# Revit family: Elite_XX_Custom
name_source: partatom
category: Windows
revit_build: Autodesk Revit 2014 (Build: 20130308_1515(x64)
units: mm (PartAtom-declared; Revit-internal decimal feet)

## types (1)
- XX_Custom
    Area Left Sash Glazing = 0.16 m²
    Area Right Sash Glazing = 0.16 m²
    Centered In Wall = Yes
    Custom Frame Offset From Exterior = 0 mm  [stored 0 ft]
    Custom Sash Width Left = 600 mm
    Custom Windload = 1000 mm  [stored 3.28084 ft]
    Custom Window Height = 590 mm  [stored 1.9357 ft]
    Custom Window Width = 890 mm  [stored 2.91995 ft]
    Default Sill Height = 800 mm
    Equal Sash Width = Yes
    Frame Thickness = 70 mm
    Glass Type = Glass
    Glazing Thickness = 4 mm  [stored 0.0131234 ft]
    Height = 590 mm  [stored 1.9357 ft]
    Inside Heavy Duty Interlocker = No
    Interlocker Configuration = 0 mm  [stored 0 ft]
    Limit Sash Height Max = 1800 mm  [stored 5.90551 ft]
    Limit Sash Height Min = 300 mm
    Limit Sash Width Left Max = 596 mm
    Limit Sash Width Left Min = 300 mm
    Limit Sash Width Max = 1500 mm  [stored 4.92126 ft]
    Limit Sash Width Min = 300 mm
    Limit Window Height Max = 1883 mm
    Limit Window Height Min = 383 mm  [stored 1.25656 ft]
    Limit Window Width Max = 2994 mm
    Limit Window Width Min = 594 mm
    Max Pane Area = 0.16 m²
    Outside Heavy Duty Interlocker = No
    Rough Width = 3 mm  [stored 0.00984252 ft]
    Sash Frame Seal = 3 mm  [stored 0.00984252 ft]
    Sash Height = 507 mm  [stored 1.66339 ft]
    Sash Side Spacing = 1 mm  [stored 0.00328084 ft]
    Sash Width Left = 448 mm
    Sash Width Right = 448 mm
    Standard Interlocker = Yes
    Wall Closure = By host
    Width = 890 mm  [stored 2.91995 ft]
    Windload Design = 1000 mm  [stored 3.28084 ft]

note: [stored X ft] marks values corroborated as IEEE doubles in the binary element streams (Revit-internal decimal feet)

## geometry (parser evidence)
native form markers: Sweep x43
no freeform markers — native parametric forms only
